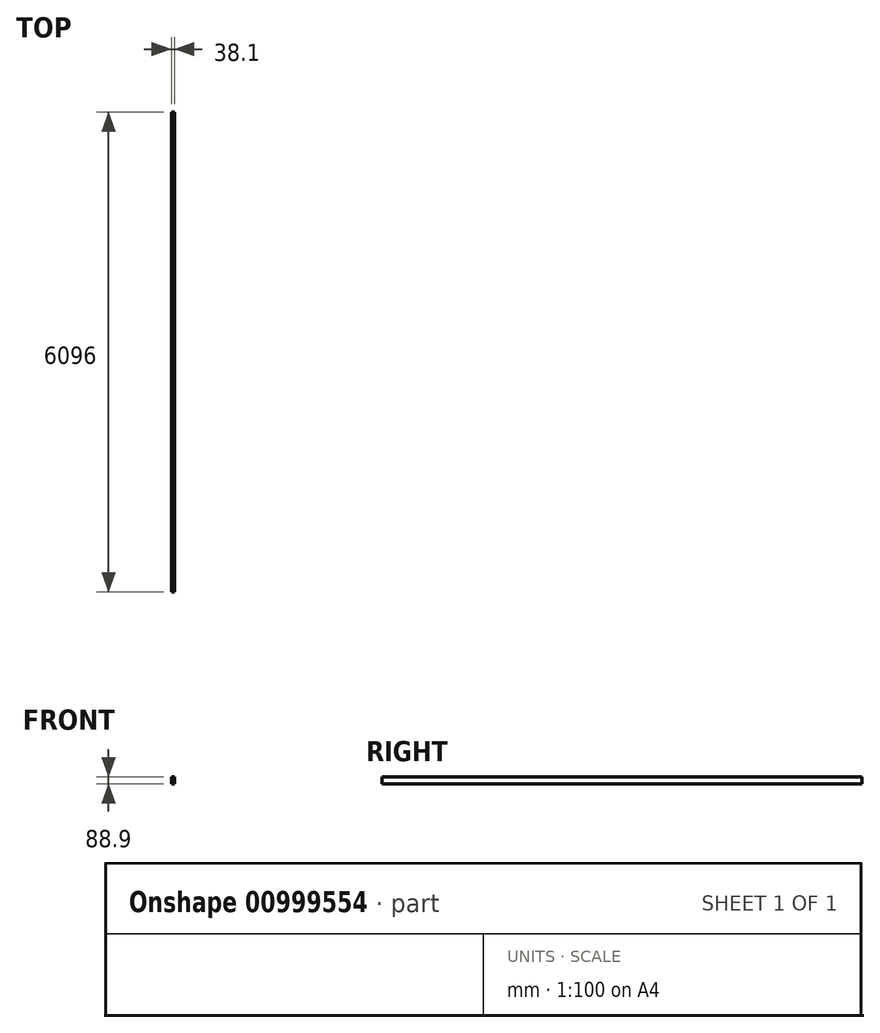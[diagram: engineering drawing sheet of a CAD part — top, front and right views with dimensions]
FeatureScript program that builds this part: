
annotation { "Feature Type Name" : "Feature", "Feature Type Description" : "" }
export const myFeature = defineFeature(function(context is Context, id is Id, definition is map)
    precondition{}
    {
        {
            var Q0;
            Q0=qCreatedBy(makeId("Front.planeOp"),FACE);
            var sketch = newSketch(context, id + "F0", { "sketchPlane" : qUnion([Q0])});
            skLineSegment(sketch, "E0.bottom", {"start": v(-65.98, 47.12) * mm, "end": v(-104.08, 47.12) * mm});
            skLineSegment(sketch, "E0.top", {"start": v(-65.98, -41.78) * mm, "end": v(-104.08, -41.78) * mm});
            skLineSegment(sketch, "E0.left", {"start": v(-65.98, 47.12) * mm, "end": v(-65.98, -41.78) * mm});
            skLineSegment(sketch, "E0.right", {"start": v(-104.08, 47.12) * mm, "end": v(-104.08, -41.78) * mm});
            skSolve(sketch);
        }
        {
            var Q0;
            Q0=makeQuery(id+"F0.imprint","IMPRINT",FACE,{"disambiguationData":[TD([[makeQuery(id+"F0.imprint","IMPRINT",EDGE,{"derivedFrom":sQuery(id+"F0.wireOp",EDGE,"E0.bottom")}),1.0]])]});
            extrude(context, id + "F1", {"entities" : qUnion([Q0]), "depth" : 6096 * mm, "offsetDistance" : 25.4 * mm});
        }
    });
